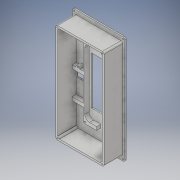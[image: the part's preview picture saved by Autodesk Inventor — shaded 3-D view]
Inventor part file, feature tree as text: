
AUTODESK INVENTOR PART (.ipt)
format: ipt  version: 2019 (Build 230136000, 136)  size: 312,320 bytes
history: native  units: in
note: dims shown in document units (in); Inventor stores cm internally (conversion verified against a paired STEP export)
features: sketch x7, extrude x5, hole x3, projected_geometry x2, fillet x1
ambient origin geometry x8: Origin, YZ Plane, XZ Plane, XY Plane, X Axis, Y Axis, Z Axis, Center Point
bodies: Solid1 (feature_tree)
feature tree (18):
  extrude  "Border"  Depth=0.1in TaperAngle=0.0deg
  extrude  "Screen Cutouts"  Depth=0.315in
  extrude  "Outer Frame"  Depth=1.75in
  extrude  "Electronic Frame"  Depth=0.125in
  hole  "Electronic Mounting Holes"  [1 undecoded]
  hole  "FrameMounting Holes"  [1 undecoded]
  extrude  "ButtonChargerCutout"  Depth=0.35in
  hole  "Outer Holes"  [1 undecoded]
  fillet  "Frame Fillet"  Radius=0.143in
  sketch  "Sketch1"  dims[d3=0.1in d4=0.0in d29=1.0in d30=0.0in]
  sketch  "Sketch5"  dims[d33=1.75in d34=0.315in]
  sketch  "Sketch6"  dims[d35=0.315in d36=1.75in]
  projected_geometry  "Projected Loop3"
  sketch  "Sketch7"  dims[d39=0.143in d40=0.125in]
  sketch  "Sketch10"  dims[d41=0.125in d42=1.373in d43=0.0in]
  sketch  "Sketch11"  dims[d45=2.33in d46=4.9in]
  projected_geometry  "Projected Loop4"
  sketch  "Sketch13"  dims[d47=0.1in d53=0.35in d54=0.31in d55=0.0in d56=0.143in d60=0.0017in d61=0.25in d62=0.125in d63=0.125in d64=0.125in d65=0.125in d76=0.1in d77=0.75in d78=0.375in d79=0.25in d80=0.5635in d81=0.35in d82=0.8108in d96=0.1in d97=0.75in d98=0.375in d99=0.25in d100=0.5635in d101=0.33in d102=0.8108in d105=0.125in d111=0.51in d112=0.31in d113=0.0in d114=0.125in d115=0.125in d116=0.125in d117=0.125in d118=0.1in d119=0.75in d120=0.375in d121=0.25in d122=0.5635in d123=1.0in d124=0.8108in d126=0.125in d127=0.3in d128=0.06in d129=0.3in d130=0.3in]
note: 3 required parameter values undecoded (feature->parameter linkage not recoverable at this tier; creation-order binding heuristic only, values carry confidence <= 0.55)
